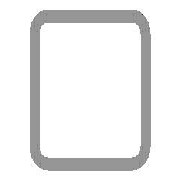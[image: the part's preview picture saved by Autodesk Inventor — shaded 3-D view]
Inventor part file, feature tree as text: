
AUTODESK INVENTOR PART (.ipt)
format: ipt  version: 2022.1 (Build 261234000, 234)  size: 548,352 bytes
history: native  units: mm (DEFAULTED — no unit token found)
features: other x17, surface_op x4, boolean_combine x2, sketch x2, sweep x1, plane x1
ambient origin geometry x8: Origin, YZ Plane, XZ Plane, XY Plane, X Axis, Y Axis, Z Axis, Center Point
bodies: Solid1 (feature_tree), Body (feature_tree)
feature tree (27):
  parser-record x1  (decoder bookkeeping rows leaked as tree rows — omitted from the tree; the rows remain in map.json)
  other  "Driven Length"
  other  "Start Plane"
  other  "End Plane"
  sweep  "Sweep Path"
  other  "Orientation Work Plane"
  surface_op  "Sculpt1"
  boolean_combine  "Combine1"
  surface_op  "Sculpt3"
  boolean_combine  "Combine3"
  sketch  "Sketch3"  dims[d7=8.0mm d9=40.0mm]
  plane  "Work Plane3"
  sketch  "Sketch4"  dims[d11=40.0mm d12=4.0mm d13=-0.0mm d14=2679.411255mm d15=20.0mm d16=20.0mm d17=90.0deg d18=2679.411255mm d19=0.0mm d20=0.0mm d111=5.0mm d112=5.0mm d113=5.0mm d114=5.0mm d115=5.0mm d116=5.0mm d117=5.0mm d118=5.0mm d119=0.0mm d120=5.0mm d121=5.0mm d122=5.0mm d123=5.0mm d124=5.0mm d125=5.0mm d126=5.0mm d127=5.0mm d128=0.0mm d129=5.0mm d130=5.0mm d131=5.0mm d132=5.0mm d133=5.0mm d134=5.0mm d135=5.0mm d136=5.0mm d137=0.0mm d138=5.0mm d139=5.0mm d140=5.0mm d141=5.0mm d142=5.0mm d143=5.0mm d144=5.0mm d145=5.0mm d146=0.0mm]
  other  "Sup17"
  other  "Sup18"
  other  "Sólido7"
  other  "Sup20"
  other  "Sup21"
  other  "Sólido8"
  surface_op  "Surface1"
  other  "Sup16"
  other  "Superficie de contorno11"
  other  "Superficie de contorno12"
  surface_op  "Surface3"
  other  "Sup19"
  other  "Superficie de contorno13"
  other  "Superficie de contorno14"
